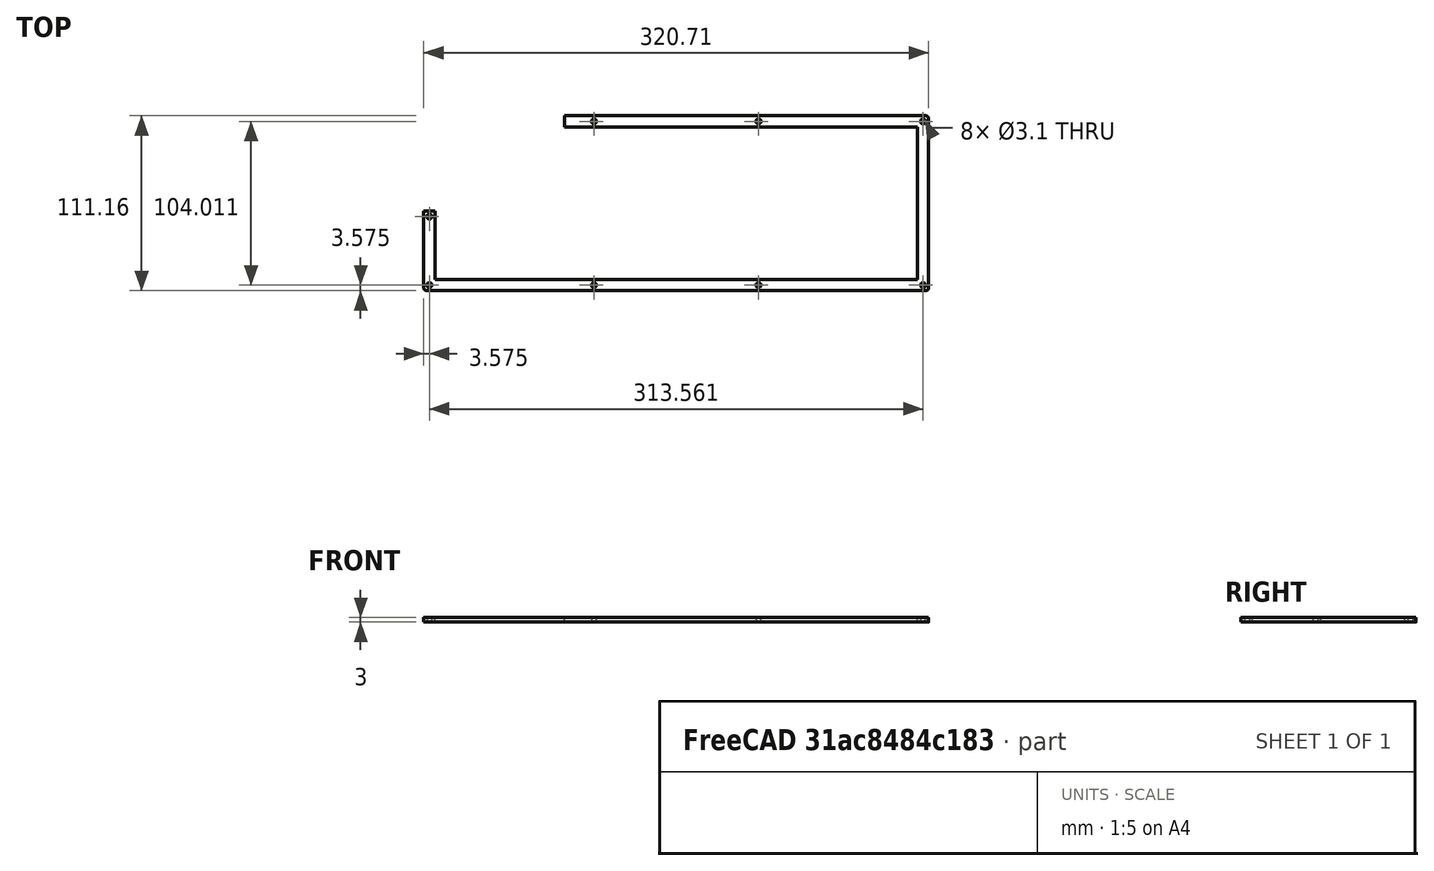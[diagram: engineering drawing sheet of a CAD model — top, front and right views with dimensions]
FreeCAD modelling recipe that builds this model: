
FCSTD DOCUMENT  (FreeCAD 0.19R24366 (Git))
Label: lower_layer
License: All rights reserved
LicenseURL: http://en.wikipedia.org/wiki/All_rights_reserved
objects: Sketcher::SketchObject×1, PartDesign::Pad×1, PartDesign::Body×1, PartDesign::CoordinateSystem×1, App::Part×1
note: 5 computed .brp shape members not serialized (recipe doc carries the construction recipe); baked Part::Feature solids carry a one-line shape summary decoded from their .brp
EXTERNAL_REF file=../master.FCStd obj=Spreadsheet

FEATURE [Sketcher::SketchObject] Sketch  label="lower_layer_sketch"
  FullyConstrained = true
  MapMode = 5
  Support = -> [XY_Plane001]
  expr: Constraints[102] = 5mm + <<master>>#<<inputs>>.raspberry_pi_4_mounting_hole_diameter / 2
  expr: Constraints[80] = <<master>>#<<inputs>>.wall_thickness
  expr: Constraints[61] = 0
  expr: Constraints[81] = <<master>>#<<inputs>>.wall_thickness
  expr: Constraints[66] = <<master>>#<<inputs>>.top_edge_padding - <<master>>#<<inputs>>.wall_thickness / 2
  expr: Constraints[8] = <<master>>#<<inputs>>.key_width
  expr: Constraints[56] = <<master>>#<<inputs>>.right_edge_padding
  expr: Constraints[82] = <<master>>#<<inputs>>.wall_thickness
  expr: Constraints[100] = <<master>>#<<inputs>>.wall_thickness
  expr: Constraints[53] = (<<master>>#<<inputs>>.key_height + <<master>>#<<inputs>>.vertical_key_spacing) * 4 + <<master>>#<<inputs>>.bottom_edge_padding - <<master>>#<<inputs>>.wall_thickness / 2 + <<master>>#<<inputs>>.key_height
  expr: Constraints[54] = <<master>>#<<inputs>>.bottom_edge_padding
  expr: Constraints[78] = <<master>>#<<inputs>>.wall_thickness / 2
  expr: Constraints[91] = <<master>>#<<inputs>>.wall_thickness / 2
  expr: Constraints[77] = <<master>>#<<inputs>>.wall_thickness / 2
  expr: Constraints[62] = ((<<master>>#<<inputs>>.key_width + <<master>>#<<inputs>>.horizontal_key_spacing) * 15 + <<master>>#<<inputs>>.key_width + <<master>>#<<inputs>>.right_edge_padding - <<master>>#<<inputs>>.wall_thickness / 2 + <<master>>#<<inputs>>.left_edge_padding - <<master>>#<<inputs>>.wall_thickness / 2) / 3
  expr: Constraints[22] = (<<master>>#<<inputs>>.key_width + <<master>>#<<inputs>>.horizontal_key_spacing) * 15
  expr: Constraints[55] = <<master>>#<<inputs>>.left_edge_padding - <<master>>#<<inputs>>.wall_thickness / 2
  expr: Constraints[9] = <<master>>#<<inputs>>.key_height
  expr: Constraints[46] = <<master>>#<<inputs>>.edge_fillet_radius
  expr: Constraints[58] = <<master>>#<<inputs>>.wall_thickness / 2
  expr: Constraints[49] = <<master>>#<<inputs>>.mounting_hole_diameter / 2
  expr: Constraints[71] = 0
  expr: Constraints[60] = 0
  expr: Constraints[35] = (<<master>>#<<inputs>>.key_height + <<master>>#<<inputs>>.vertical_key_spacing) * 4
  expr: Constraints[85] = <<master>>#<<inputs>>.wall_thickness
  expr: Constraints[94] = <<master>>#<<inputs>>.hyperpixel_width
  expr: Constraints[73] = 0
  expr: Constraints[59] = ((<<master>>#<<inputs>>.key_width + <<master>>#<<inputs>>.horizontal_key_spacing) * 15 + <<master>>#<<inputs>>.key_width + <<master>>#<<inputs>>.right_edge_padding - <<master>>#<<inputs>>.wall_thickness / 2 + <<master>>#<<inputs>>.left_edge_padding - <<master>>#<<inputs>>.wall_thickness / 2) / 3
  expr: Constraints[74] = (<<master>>#<<inputs>>.key_height + <<master>>#<<inputs>>.vertical_key_spacing) * 3 - <<master>>#<<inputs>>.wall_thickness / 2
  expr: Constraints[95] = <<master>>#<<inputs>>.raspberry_pi_4_mounting_hole_diameter
  expr: Constraints[97] = <<master>>#<<inputs>>.hyperpixel_top_hole_padding
  expr: Constraints[96] = <<master>>#<<inputs>>.hyperpixel_right_hole_padding
  sketch-geometry (36):
    g0: LineSegment StartX=-7 StartY=7 StartZ=0 EndX=7 EndY=7 EndZ=0
    g1: LineSegment StartX=7 StartY=7 StartZ=0 EndX=7 EndY=-7 EndZ=0
    g2: LineSegment StartX=7 StartY=-7 StartZ=0 EndX=-7 EndY=-7 EndZ=0
    g3: LineSegment StartX=-7 StartY=-7 StartZ=0 EndX=-7 EndY=7 EndZ=0
    g4: LineSegment StartX=278.75 StartY=7 StartZ=0 EndX=292.75 EndY=7 EndZ=0
    g5: LineSegment StartX=292.75 StartY=7 StartZ=0 EndX=292.75 EndY=-7 EndZ=0
    g6: LineSegment StartX=292.75 StartY=-7 StartZ=0 EndX=278.75 EndY=-7 EndZ=0
    g7: LineSegment StartX=278.75 StartY=-7 StartZ=0 EndX=278.75 EndY=7 EndZ=0
    g8: GeomPoint X=278.75 Y=7 Z=0
    g9: LineSegment StartX=-7 StartY=-69.2 StartZ=0 EndX=7 EndY=-69.2 EndZ=0
    g10: LineSegment StartX=7 StartY=-69.2 StartZ=0 EndX=7 EndY=-83.2 EndZ=0
    g11: LineSegment StartX=7 StartY=-83.2 StartZ=0 EndX=-7 EndY=-83.2 EndZ=0
    g12: LineSegment StartX=-7 StartY=-83.2 StartZ=0 EndX=-7 EndY=-69.2 EndZ=0
    g13: LineSegment StartX=71.8975 StartY=17.4775 StartZ=0 EndX=301.228 EndY=17.4775 EndZ=0
    g14: LineSegment StartX=303.228 StartY=15.4775 StartZ=0 EndX=303.228 EndY=-91.6775 EndZ=0
    g15: LineSegment StartX=301.228 StartY=-93.6775 StartZ=0 EndX=-15.4775 EndY=-93.6775 EndZ=0
    g16: LineSegment StartX=-17.4775 StartY=-91.6775 StartZ=0 EndX=-17.4775 EndY=-43.006 EndZ=0
    g17: ArcOfCircle CenterX=301.228 CenterY=15.4775 CenterZ=0 NormalX=0 NormalY=0 NormalZ=1 AngleXU=0 Radius=2 StartAngle=0 EndAngle=1.5708
    g18: ArcOfCircle CenterX=301.228 CenterY=-91.6775 CenterZ=0 NormalX=0 NormalY=0 NormalZ=1 AngleXU=0 Radius=2 StartAngle=4.71239 EndAngle=6.28319
    g19: ArcOfCircle CenterX=-15.4775 CenterY=-91.6775 CenterZ=0 NormalX=0 NormalY=0 NormalZ=1 AngleXU=0 Radius=2 StartAngle=3.14159 EndAngle=4.71239
    g20: Circle CenterX=-13.9055 CenterY=-90.1055 CenterZ=0 NormalX=0 NormalY=0 NormalZ=1 AngleXU=0 Radius=1.55
    g21: Circle CenterX=195.135 CenterY=-90.1055 CenterZ=0 NormalX=0 NormalY=0 NormalZ=1 AngleXU=0 Radius=1.55
    g22: Circle CenterX=299.656 CenterY=-90.1055 CenterZ=0 NormalX=0 NormalY=0 NormalZ=1 AngleXU=0 Radius=1.55
    g23: Circle CenterX=90.6148 CenterY=-90.1055 CenterZ=0 NormalX=0 NormalY=0 NormalZ=1 AngleXU=0 Radius=1.55
    g24: Circle CenterX=90.6148 CenterY=13.9055 CenterZ=0 NormalX=0 NormalY=0 NormalZ=1 AngleXU=0 Radius=1.55
    g25: Circle CenterX=195.135 CenterY=13.9055 CenterZ=0 NormalX=0 NormalY=0 NormalZ=1 AngleXU=0 Radius=1.55
    g26: Circle CenterX=299.656 CenterY=13.9055 CenterZ=0 NormalX=0 NormalY=0 NormalZ=1 AngleXU=0 Radius=1.55
    g27: Circle CenterX=-13.9055 CenterY=-46.578 CenterZ=0 NormalX=0 NormalY=0 NormalZ=1 AngleXU=0 Radius=1.55
    g28: LineSegment StartX=-17.4775 StartY=-43.006 StartZ=0 EndX=-10.3335 EndY=-43.006 EndZ=0
    g29: LineSegment StartX=-10.3335 StartY=-86.5335 StartZ=0 EndX=296.084 EndY=-86.5335 EndZ=0
    g30: LineSegment StartX=296.084 StartY=10.3335 StartZ=0 EndX=296.084 EndY=-86.5335 EndZ=0
    g31: LineSegment StartX=71.8975 StartY=10.3335 StartZ=0 EndX=296.084 EndY=10.3335 EndZ=0
    g32: LineSegment StartX=-10.3335 StartY=-43.006 StartZ=0 EndX=-10.3335 EndY=-86.5335 EndZ=0
    g33: LineSegment StartX=-17.4775 StartY=-43.006 StartZ=0 EndX=80.5225 EndY=-43.006 EndZ=0
    g34: Circle CenterX=65.5225 CenterY=12.9775 CenterZ=0 NormalX=0 NormalY=0 NormalZ=1 AngleXU=0 Radius=2.75
    g35: LineSegment StartX=71.8975 StartY=17.4775 StartZ=0 EndX=71.8975 EndY=10.3335 EndZ=0
  constraints (103):
    c: Coincident(g0,g1)
    c: Coincident(g1,g2)
    c: Coincident(g2,g3)
    c: Coincident(g3,g0)
    c: Horizontal(g0)
    c: Horizontal(g2)
    c: Vertical(g1)
    c: Vertical(g3)
    c: Distance(g0) = 14
    c: Distance(g3) = 14
    c: Symmetric(g0,g1,g-1)
    c: Coincident(g4,g5)
    c: Coincident(g5,g6)
    c: Coincident(g6,g7)
    c: Coincident(g7,g4)
    c: Horizontal(g4)
    c: Horizontal(g6)
    c: Vertical(g5)
    c: Vertical(g7)
    c: Equal(g3,g7)
    c: Equal(g0,g4)
    c: DistanceY(g0,g8) = 0
    c: DistanceX(g0,g8) = 285.75
    c: Coincident(g4,g8)
    c: Coincident(g9,g10)
    c: Coincident(g10,g11)
    c: Coincident(g11,g12)
    c: Coincident(g12,g9)
    c: Horizontal(g9)
    c: Horizontal(g11)
    c: Vertical(g10)
    c: Vertical(g12)
    c: Equal(g0,g9)
    c: Equal(g3,g12)
    c: DistanceX(g0,g9) = 0
    c: DistanceY(g9,g0) = 76.2
    c: Horizontal(g13)
    c: Horizontal(g15)
    c: Vertical(g14)
    c: Vertical(g16)
    c: Tangent(g13,g17) = 1.5708
    c: Tangent(g14,g17) = 1.5708
    c: Tangent(g14,g18) = 1.5708
    c: Tangent(g15,g18) = 1.5708
    c: Tangent(g15,g19) = 1.5708
    c: Tangent(g16,g19) = 1.5708
    c: Radius(g19) = 2
    c: Equal(g19,g18)
    c: Equal(g17,g18)
    c: Radius(g20) = 1.55
    c: Equal(g20,g21)
    c: Equal(g21,g22)
    c: Equal(g21,g23)
    c: DistanceY(g20,g0) = 97.1055
    c: DistanceY(g15,g11) = 10.4775
    c: DistanceX(g20,g0) = 6.9055
    c: DistanceX(g4,g14) = 10.4775
    c: DistanceY(g20,g22) = 0
    c: DistanceX(g22,g14) = 3.572
    c: DistanceX(g20,g23) = 104.52
    c: DistanceY(g23,g20) = 0
    c: DistanceY(g23,g21) = 0
    c: DistanceX(g21,g22) = 104.52
    c: Equal(g21,g26)
    c: Equal(g26,g25)
    c: Equal(g26,g24)
    c: DistanceY(g8,g26) = 6.9055
    c: DistanceX(g26,g22) = 0
    c: DistanceX(g25,g21) = 0
    c: DistanceY(g25,g26) = 0
    c: DistanceX(g23,g24) = 0
    c: DistanceY(g24,g25) = 0
    c: Equal(g20,g27)
    c: DistanceX(g20,g27) = 0
    c: DistanceY(g27,g0) = 53.578
    c: Horizontal(g28)
    c: Coincident(g16,g28)
    c: DistanceX(g16,g27) = 3.572
    c: DistanceY(g26,g13) = 3.572
    c: Horizontal(g29)
    c: DistanceY(g15,g29) = 7.144
    c: DistanceX(g16,g29) = 7.144
    c: DistanceX(g29,g14) = 7.144
    c: Vertical(g30)
    c: Coincident(g30,g29)
    c: DistanceY(g30,g13) = 7.144
    c: Horizontal(g31)
    c: Coincident(g31,g30)
    c: Vertical(g32)
    c: Coincident(g32,g29)
    c: Coincident(g28,g32)
    c: DistanceY(g27,g28) = 3.572
    c: Horizontal(g33)
    c: Coincident(g33,g16)
    c: Distance(g33) = 98
    c: Radius(g34) = 2.75
    c: DistanceX(g34,g33) = 15
    c: DistanceY(g34,g13) = 4.5
    c: DistanceX(g13,g31) = 0
    c: Coincident(g35,g13)
    c: Distance(g35) = 7.144
    c: Perpendicular(g13,g35)
    c: DistanceX(g34,g13) = 6.375
FEATURE [PartDesign::Pad] Pad  label="lower_layer_pad"
  Direction = (1,1,1)
  Length = 3
  Length2 = 100
  Profile = -> Sketch
  Type = 0
  expr: Length = <<master>>#<<inputs>>.lower_layer_thickness
FEATURE [PartDesign::Body] Body  label="lower_layer_body"
  Group = -> [Sketch,Pad]
  Origin = -> Origin001
  Tip = -> Pad
FEATURE [PartDesign::CoordinateSystem] top_left_lcs_closed_layer  label="lower_layer_lcs"
  AttacherType = Attacher::AttachEngine3D
  MapMode = 5
  Placement = pos=(0,0,3) rot=(0,0,1;0rad)
  Support = -> [Pad]
FEATURE [App::Part] Part  label="lower_layer_part"
  Group = -> [Body,top_left_lcs_closed_layer]
  Origin = -> Origin
